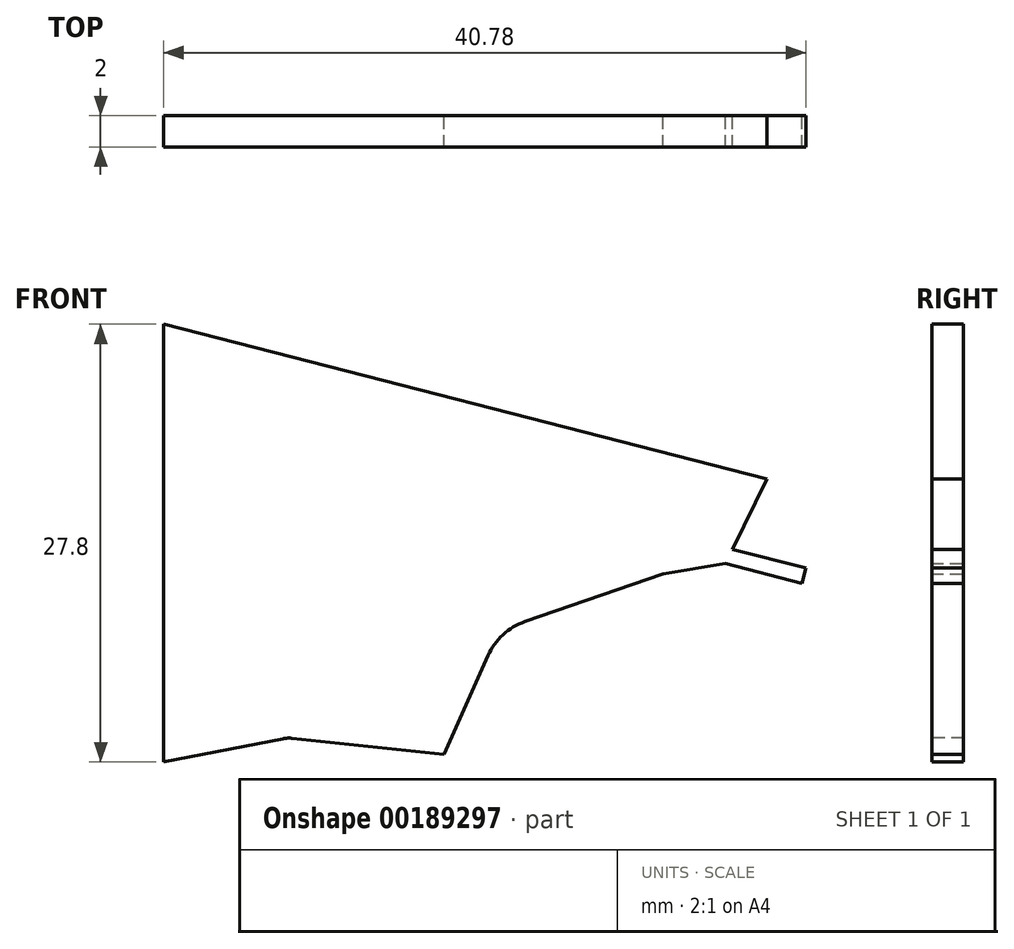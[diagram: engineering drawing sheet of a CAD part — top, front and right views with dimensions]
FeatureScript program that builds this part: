
annotation { "Feature Type Name" : "Feature", "Feature Type Description" : "" }
export const myFeature = defineFeature(function(context is Context, id is Id, definition is map)
    precondition{}
    {
        {
            var Q0;
            Q0=qCreatedBy(makeId("Front.planeOp"),FACE);
            var sketch = newSketch(context, id + "F0", { "sketchPlane" : qUnion([Q0])});
            skLineSegment(sketch, "E0", {"start": v(-10.46, -15.49) * mm, "end": v(-2.6, -13.96) * mm});
            skLineSegment(sketch, "E1", {"start": v(27.86, 2.5) * mm, "end": v(25.67, -1.98) * mm});
            skLineSegment(sketch, "E2", {"start": v(-10.46, 12.31) * mm, "end": v(-10.46, -15.49) * mm});
            skLineSegment(sketch, "E3", {"start": v(-10.46, 12.31) * mm, "end": v(27.86, 2.5) * mm});
            skLineSegment(sketch, "E4", {"start": v(-2.6, -13.96) * mm, "end": v(7.34, -15) * mm});
            skLineSegment(sketch, "E5", {"start": v(7.34, -15) * mm, "end": v(10.84, -7.15) * mm});
            skLineSegment(sketch, "E6", {"start": v(10.84, -7.15) * mm, "end": v(21.24, -3.57) * mm});
            skLineSegment(sketch, "E7", {"start": v(21.24, -3.57) * mm, "end": v(25.23, -2.9) * mm});
            skLineSegment(sketch, "E8", {"start": v(25.23, -2.9) * mm, "end": v(30.07, -4.14) * mm});
            skLineSegment(sketch, "E9", {"start": v(30.07, -4.14) * mm, "end": v(30.32, -3.17) * mm});
            skLineSegment(sketch, "E10", {"start": v(30.32, -3.17) * mm, "end": v(25.67, -1.98) * mm});
            skSolve(sketch);
        }
        {
            var Q0;
            Q0=makeQuery(id+"F0.imprint","IMPRINT",FACE,{"disambiguationData":[TD([[makeQuery(id+"F0.imprint","IMPRINT",EDGE,{"derivedFrom":sQuery(id+"F0.wireOp",EDGE,"E0")}),1.0]])]});
            extrude(context, id + "F1", {"entities" : qUnion([Q0]), "depth" : 2 * mm, "offsetDistance" : 25 * mm});
        }
        {
            var Q0;
            Q0=makeQuery(id+"F1.opExtrude","SWEPT_EDGE",EDGE,{"disambiguationData":[OSD([sQuery(id+"F0.wireOp",EDGE,"E5"),sQuery(id+"F0.wireOp",EDGE,"E6")])]});
            fillet(context, id + "F2", {"entities" : qUnion([Q0]), "tangentPropagation" : true, "radius" : 4 * mm, "defaultsChanged" : true, "vertexSettings" : [], "allowEdgeOverflow" : false});
        }
        {
            var Q0;
            Q0=makeQuery(id+"F1.opExtrude","SWEPT_EDGE",EDGE,{"disambiguationData":[OSD([sQuery(id+"F0.wireOp",EDGE,"E0"),sQuery(id+"F0.wireOp",EDGE,"E4")])]});
            fillet(context, id + "F3", {"entities" : qUnion([Q0]), "tangentPropagation" : true, "radius" : 2 * mm, "defaultsChanged" : true, "vertexSettings" : [], "allowEdgeOverflow" : false});
        }
    });
